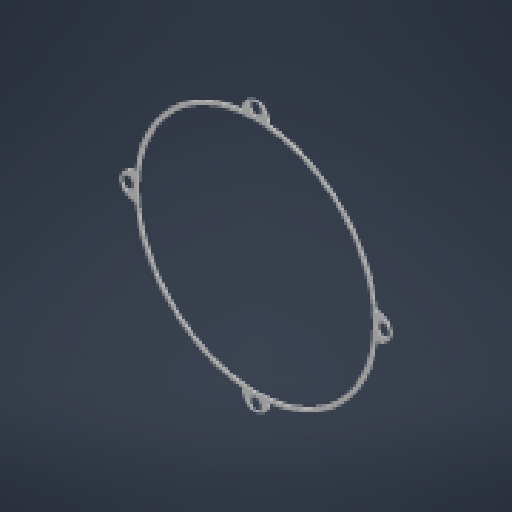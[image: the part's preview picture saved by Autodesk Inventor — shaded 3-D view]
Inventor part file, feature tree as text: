
AUTODESK INVENTOR PART (.ipt)
format: ipt  version: 2024.2 (Build 282272000, 272)  size: 176,128 bytes
history: native  units: in
note: dims shown in document units (in); Inventor stores cm internally (conversion verified against a paired STEP export)
features: other x4, extrude x2, sketch x2, reference x1
ambient origin geometry x8: Origin, YZ Plane, XZ Plane, XY Plane, X Axis, Y Axis, Z Axis, Center Point
bodies: Solid1 (feature_tree)
feature tree (9):
  extrude  "Extrusion1"  TaperAngle=0.0deg  [1 undecoded]
  extrude  "Extrusion2"  Depth=1.75in
  sketch  "Sketch1"  dims[d0=0.0591in d1=0.0in]
  reference  "Reference1"
  sketch  "Sketch2"  dims[d2=3.5in d3=1.75in d4=3.5in d5=0.0in d6=1.75in d7=0.4331in d8=0.4331in d9=0.4331in d10=0.4331in d11=0.0394in d12=0.0in d13=0.1693in d14=0.0985in d15=0.0in d16=0.1693in d17=0.1693in d18=0.1693in d19=0.0in d20=0.0985in d21=0.0in d22=0.0985in d23=0.0in d24=0.0985in d25=0.0in d26=0.0in]
  other  "<userpath>\Desktop\Robotics\Swerve2\Assemblies\Pod.iam"
  other  "Pod.iam"
  other  "3ID3.5OD_Bearing:1"
  parser-record x1  (decoder bookkeeping rows leaked as tree rows — omitted from the tree; the rows remain in map.json)
note: 1 required parameter value undecoded (feature->parameter linkage not recoverable at this tier; creation-order binding heuristic only, values carry confidence <= 0.55)
